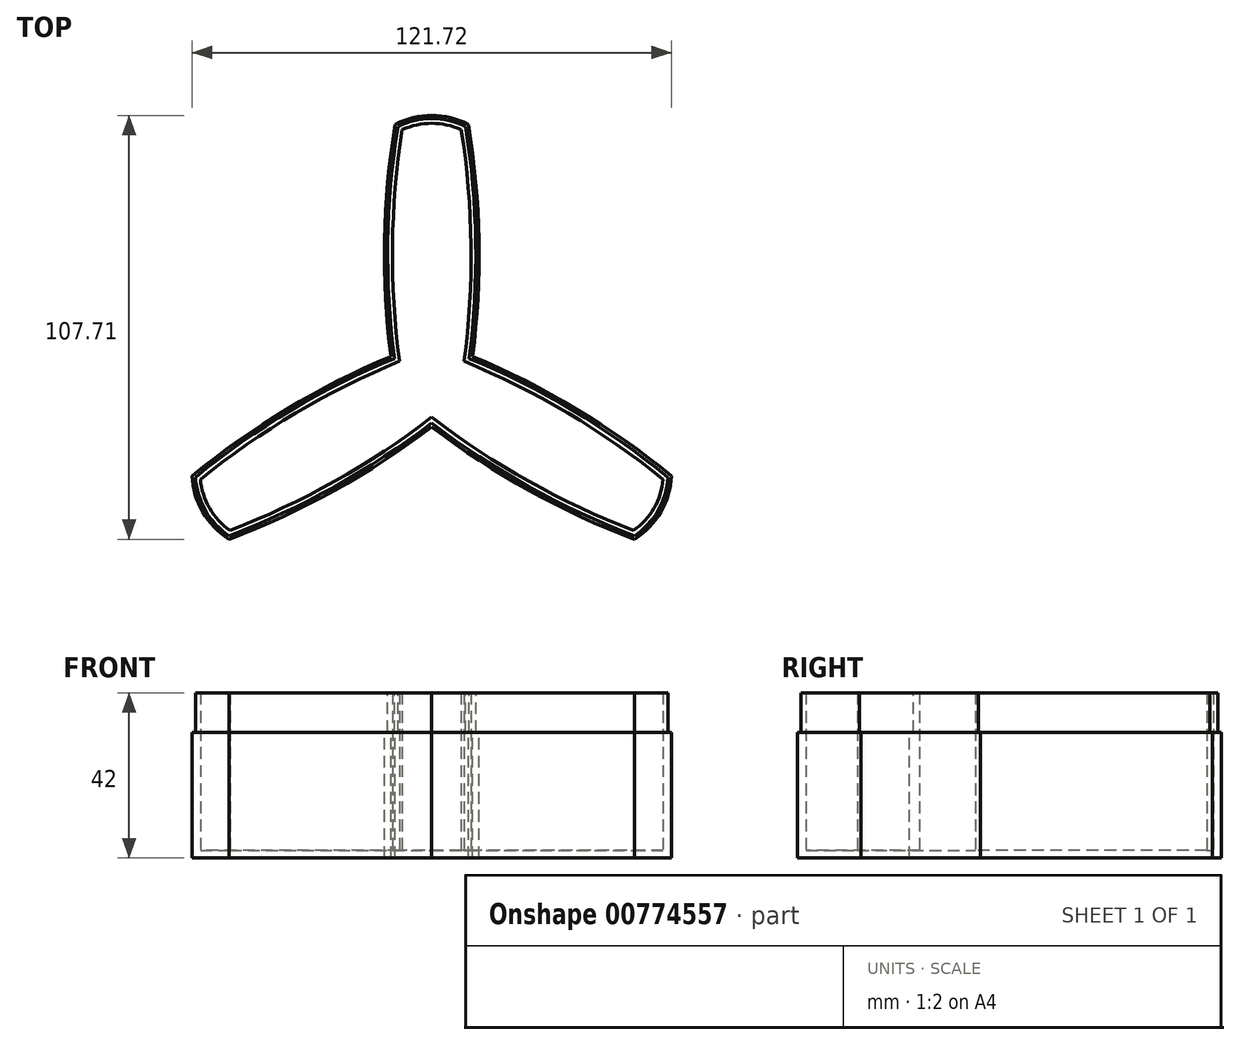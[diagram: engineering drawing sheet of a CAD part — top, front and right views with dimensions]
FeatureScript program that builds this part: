
annotation { "Feature Type Name" : "Feature", "Feature Type Description" : "" }
export const myFeature = defineFeature(function(context is Context, id is Id, definition is map)
    precondition{}
    {
        {
            var Q0;
            Q0=qCreatedBy(makeId("Top.planeOp"),FACE);
            var sketch = newSketch(context, id + "F0", { "sketchPlane" : qUnion([Q0])});
            skCircle(sketch, "E0", {"center": v(0, 0) * mm, "radius": 7.5 * mm});
            skCircle(sketch, "E1", {"center": v(0, 0) * mm, "radius": 64 * mm, "construction": true});
            skLineSegment(sketch, "E2", {"start": v(0, 64) * mm, "end": v(0, 0) * mm, "construction": true});
            skPoint(sketch, "E3", {"position": v(7.5, 63.56) * mm});
            skPoint(sketch, "E4.MirrorP", {"position": v(-7.5, 63.56) * mm});
            skArc(sketch, "E5", {"start": v(7.5, 63.56) * mm, "mid": v(0, 65.2) * mm, "end": v(-7.5, 63.56) * mm});
            skArc(sketch, "E6", {"start": v(8.2, 4.73) * mm, "mid": v(9.99, 34.17) * mm, "end": v(7.5, 63.56) * mm});
            skArc(sketch, "E7.MirrorCS", {"start": v(-8.2, 4.73) * mm, "mid": v(-9.99, 34.17) * mm, "end": v(-7.5, 63.56) * mm});
            skLineSegment(sketch, "E8", {"start": v(-71.33, 41.18) * mm, "end": v(-10.37, 5.99) * mm, "construction": true});
            skLineSegment(sketch, "E9", {"start": v(67.42, 38.92) * mm, "end": v(-67.66, -39.06) * mm, "construction": true});
            skPoint(sketch, "E10.MirrorP", {"position": v(-58.8, -25.28) * mm});
            skArc(sketch, "E11.MirrorCS", {"start": v(-51.3, -38.27) * mm, "mid": v(-56.46, -32.6) * mm, "end": v(-58.8, -25.28) * mm});
            skArc(sketch, "E12.MirrorCS", {"start": v(-8.2, 4.73) * mm, "mid": v(-34.58, -8.44) * mm, "end": v(-58.8, -25.28) * mm});
            skArc(sketch, "E13.MirrorCS", {"start": v(0, -9.46) * mm, "mid": v(-24.6, -25.73) * mm, "end": v(-51.3, -38.27) * mm});
            skArc(sketch, "E14.MirrorCS", {"start": v(0, -9.46) * mm, "mid": v(24.6, -25.73) * mm, "end": v(51.3, -38.27) * mm});
            skArc(sketch, "E15.MirrorCS", {"start": v(8.2, 4.73) * mm, "mid": v(34.58, -8.44) * mm, "end": v(58.8, -25.28) * mm});
            skArc(sketch, "E16.MirrorCS", {"start": v(58.8, -25.28) * mm, "mid": v(56.46, -32.6) * mm, "end": v(51.3, -38.27) * mm});
            skArc(sketch, "E17.0", {"start": v(10.37, 5.99) * mm, "mid": v(11.97, 35.48) * mm, "end": v(9.31, 64.9) * mm});
            skArc(sketch, "E17.1", {"start": v(9.31, 64.9) * mm, "mid": v(0, 67.2) * mm, "end": v(-9.31, 64.9) * mm});
            skArc(sketch, "E17.2", {"start": v(-10.37, 5.99) * mm, "mid": v(-11.97, 35.48) * mm, "end": v(-9.31, 64.9) * mm});
            skArc(sketch, "E18.MirrorCS", {"start": v(10.37, 5.99) * mm, "mid": v(36.71, -7.38) * mm, "end": v(60.86, -24.38) * mm});
            skArc(sketch, "E19.MirrorCS", {"start": v(0, -11.98) * mm, "mid": v(24.74, -28.1) * mm, "end": v(51.55, -40.51) * mm});
            skArc(sketch, "E20.MirrorCS", {"start": v(60.86, -24.38) * mm, "mid": v(58.2, -33.6) * mm, "end": v(51.55, -40.51) * mm});
            skArc(sketch, "E21.MirrorCS", {"start": v(0, -11.98) * mm, "mid": v(-24.74, -28.1) * mm, "end": v(-51.55, -40.51) * mm});
            skArc(sketch, "E22.MirrorCS", {"start": v(-10.37, 5.99) * mm, "mid": v(-36.71, -7.38) * mm, "end": v(-60.86, -24.38) * mm});
            skArc(sketch, "E23.MirrorCS", {"start": v(-51.55, -40.51) * mm, "mid": v(-58.2, -33.6) * mm, "end": v(-60.86, -24.38) * mm});
            skPoint(sketch, "E24.orphan", {"position": v(-16.32, 3.38) * mm});
            skPoint(sketch, "E25.orphan", {"position": v(-3.75, 6.5) * mm});
            skPoint(sketch, "E26.orphan", {"position": v(-7.5, 0) * mm});
            skPoint(sketch, "E27.orphan", {"position": v(-11.09, 12.45) * mm});
            skLineSegment(sketch, "E28.trimOffspring", {"start": v(-8.2, 4.73) * mm, "end": v(57.36, -33.12) * mm, "construction": true});
            skPoint(sketch, "E29.orphan", {"position": v(5.24, -15.83) * mm});
            skPoint(sketch, "E30.orphan", {"position": v(-3.75, -6.5) * mm});
            skPoint(sketch, "E31.orphan", {"position": v(3.75, -6.5) * mm});
            skPoint(sketch, "E32.orphan", {"position": v(-5.24, -15.83) * mm});
            skPoint(sketch, "E33.orphan", {"position": v(3.75, 6.5) * mm});
            skPoint(sketch, "E34.orphan", {"position": v(16.32, 3.38) * mm});
            skPoint(sketch, "E35.orphan", {"position": v(7.5, 0) * mm});
            skPoint(sketch, "E36.orphan", {"position": v(11.09, 12.45) * mm});
            skSolve(sketch);
        }
        {
            var Q0;
            Q0 = qSketchRegion(id + "F0", true);
            var Q1;
            Q1=makeQuery(id+"F0.imprint","IMPRINT",FACE,{"disambiguationData":[TD([[makeQuery(id+"F0.imprint","IMPRINT",EDGE,{"derivedFrom":sQuery(id+"F0.wireOp",EDGE,"E0")}),-1.0]])]});
            var Q2;
            Q2=makeQuery(id+"F0.imprint","IMPRINT",FACE,{"disambiguationData":[TD([[makeQuery(id+"F0.imprint","IMPRINT",EDGE,{"derivedFrom":sQuery(id+"F0.wireOp",EDGE,"E0")}),1.0]])]});
            extrude(context, id + "F1", {"entities" : qUnion([Q0, Q1, Q2]), "oppositeDirection" : true, "depth" : 2 * mm, "offsetDistance" : 25 * mm});
        }
        {
            var Q0;
            Q0=makeQuery(id+"F0.imprint","IMPRINT",FACE,{"disambiguationData":[TD([[makeQuery(id+"F0.imprint","IMPRINT",EDGE,{"derivedFrom":sQuery(id+"F0.wireOp",EDGE,"E5")}),-1.0]])]});
            extrude(context, id + "F2", {"entities" : qUnion([Q0]), "operationType" : NewBodyOperationType.ADD, "depth" : 40 * mm, "offsetDistance" : 25 * mm});
        }
        {
            var Q0;
            Q0=makeQuery(id+"F2.opExtrude","CAP_FACE",FACE,{"disambiguationData":[OSD([sQuery(id+"F0.wireOp",EDGE,"E5"),sQuery(id+"F0.wireOp",EDGE,"E6"),sQuery(id+"F0.wireOp",EDGE,"E7.MirrorCS"),sQuery(id+"F0.wireOp",EDGE,"E11.MirrorCS"),sQuery(id+"F0.wireOp",EDGE,"E12.MirrorCS"),sQuery(id+"F0.wireOp",EDGE,"E13.MirrorCS"),sQuery(id+"F0.wireOp",EDGE,"E14.MirrorCS"),sQuery(id+"F0.wireOp",EDGE,"E15.MirrorCS"),sQuery(id+"F0.wireOp",EDGE,"E16.MirrorCS"),sQuery(id+"F0.wireOp",EDGE,"E17.0"),sQuery(id+"F0.wireOp",EDGE,"E17.1"),sQuery(id+"F0.wireOp",EDGE,"E17.2"),sQuery(id+"F0.wireOp",EDGE,"E18.MirrorCS"),sQuery(id+"F0.wireOp",EDGE,"E19.MirrorCS"),sQuery(id+"F0.wireOp",EDGE,"E20.MirrorCS"),sQuery(id+"F0.wireOp",EDGE,"E21.MirrorCS"),sQuery(id+"F0.wireOp",EDGE,"E22.MirrorCS"),sQuery(id+"F0.wireOp",EDGE,"E23.MirrorCS")])],"isStart":false});
            var sketch = newSketch(context, id + "F3", { "sketchPlane" : qUnion([Q0])});
            skArc(sketch, "E37.0", {"start": v(0, -10.97) * mm, "mid": v(24.69, -27.16) * mm, "end": v(51.45, -39.62) * mm});
            skArc(sketch, "E37.1", {"start": v(60.04, -24.75) * mm, "mid": v(57.5, -33.2) * mm, "end": v(51.45, -39.62) * mm});
            skArc(sketch, "E37.2", {"start": v(0, -10.97) * mm, "mid": v(-24.69, -27.16) * mm, "end": v(-51.45, -39.62) * mm});
            skArc(sketch, "E37.3", {"start": v(9.5, 5.49) * mm, "mid": v(35.86, -7.8) * mm, "end": v(60.04, -24.75) * mm});
            skArc(sketch, "E37.4", {"start": v(9.5, 5.49) * mm, "mid": v(11.18, 34.96) * mm, "end": v(8.59, 64.37) * mm});
            skArc(sketch, "E37.5", {"start": v(-51.45, -39.62) * mm, "mid": v(-57.5, -33.2) * mm, "end": v(-60.04, -24.75) * mm});
            skArc(sketch, "E37.6", {"start": v(-9.5, 5.49) * mm, "mid": v(-35.86, -7.8) * mm, "end": v(-60.04, -24.75) * mm});
            skArc(sketch, "E37.7", {"start": v(-9.5, 5.49) * mm, "mid": v(-11.18, 34.96) * mm, "end": v(-8.59, 64.37) * mm});
            skArc(sketch, "E37.8", {"start": v(8.59, 64.37) * mm, "mid": v(0, 66.4) * mm, "end": v(-8.59, 64.37) * mm});
            skSolve(sketch);
        }
        {
            var Q0;
            Q0=makeQuery(id+"F3.imprint","IMPRINT",FACE,{"disambiguationData":[TD([[makeQuery(id+"F3.imprint","IMPRINT",EDGE,{"derivedFrom":sQuery(id+"F3.wireOp",EDGE,"E37.0")}),-1.0]])]});
            extrude(context, id + "F4", {"entities" : qUnion([Q0]), "operationType" : NewBodyOperationType.REMOVE, "oppositeDirection" : true, "depth" : 10 * mm, "offsetDistance" : 25 * mm});
        }
    });
